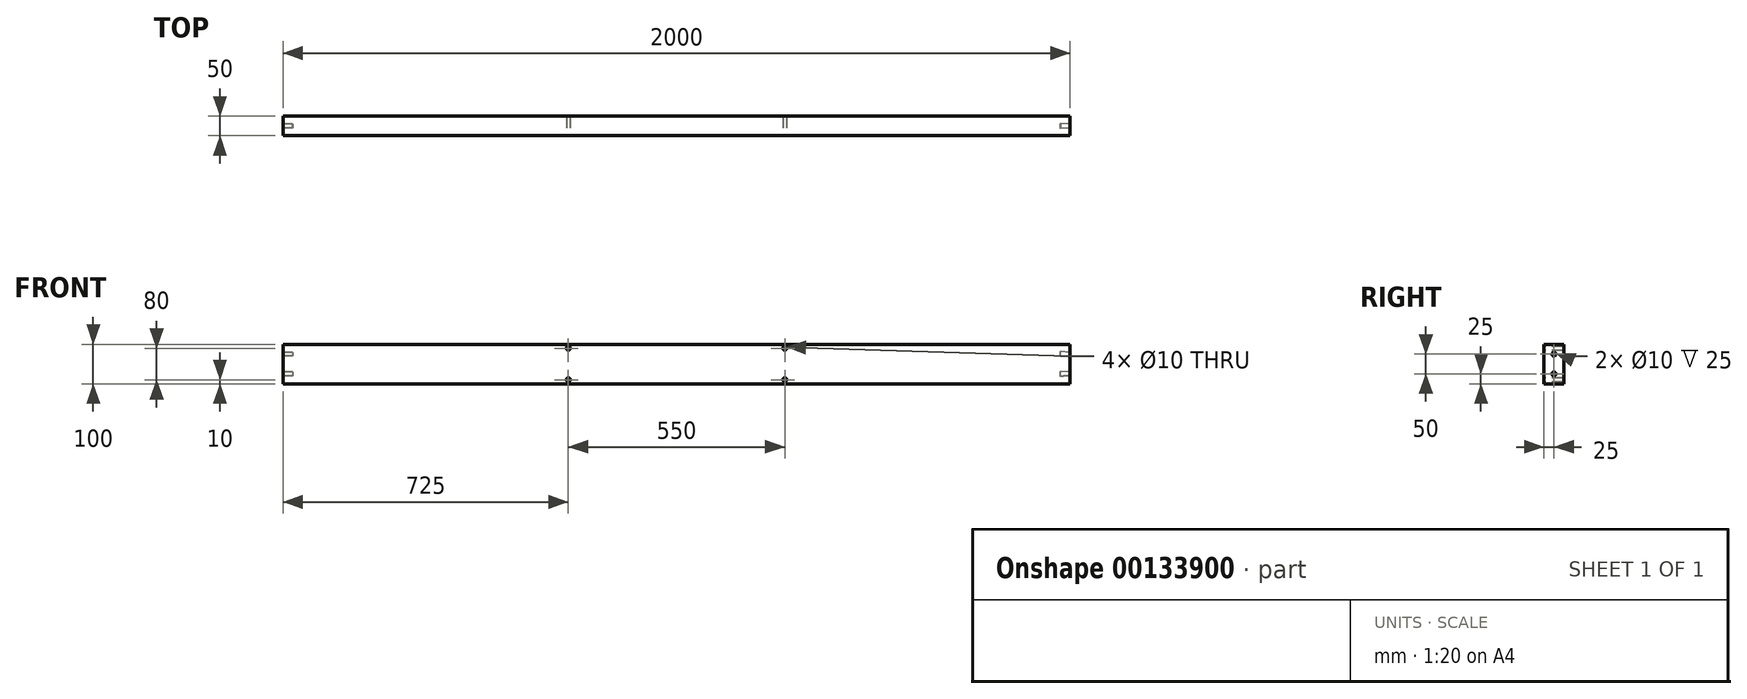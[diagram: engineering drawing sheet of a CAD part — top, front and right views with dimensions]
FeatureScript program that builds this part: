
annotation { "Feature Type Name" : "Feature", "Feature Type Description" : "" }
export const myFeature = defineFeature(function(context is Context, id is Id, definition is map)
    precondition{}
    {
        {
            var Q0;
            Q0=qCreatedBy(makeId("Front.planeOp"),FACE);
            var sketch = newSketch(context, id + "F0", { "sketchPlane" : qUnion([Q0])});
            skLineSegment(sketch, "E0.bottom", {"start": v(1000, -50) * mm, "end": v(-1000, -50) * mm});
            skLineSegment(sketch, "E0.top", {"start": v(1000, 50) * mm, "end": v(-1000, 50) * mm});
            skLineSegment(sketch, "E0.left", {"start": v(1000, -50) * mm, "end": v(1000, 50) * mm});
            skLineSegment(sketch, "E0.right", {"start": v(-1000, -50) * mm, "end": v(-1000, 50) * mm});
            skPoint(sketch, "E0.middle", {"position": v(0, 0) * mm});
            skSolve(sketch);
        }
        {
            var Q0;
            Q0=qSketchRegion(id+"F0",true);
            extrude(context, id + "F1", {"entities" : qUnion([Q0]), "depth" : 50 * mm});
        }
        {
            var Q0;
            Q0=makeQuery(id+"F1.opExtrude","SWEPT_FACE",FACE,{"disambiguationData":[OSD([sQuery(id+"F0.wireOp",EDGE,"E0.left")])]});
            var sketch = newSketch(context, id + "F2", { "sketchPlane" : qUnion([Q0])});
            skCircle(sketch, "E1", {"center": v(-25, 25) * mm, "radius": 5 * mm});
            skPoint(sketch, "E1.centerSnap0", {"position": v(-25, 50) * mm});
            skCircle(sketch, "E2", {"center": v(-25, -25) * mm, "radius": 5 * mm});
            skSolve(sketch);
        }
        {
            var Q0;
            Q0=makeQuery(id+"F1.opExtrude","SWEPT_FACE",FACE,{"disambiguationData":[OSD([sQuery(id+"F0.wireOp",EDGE,"E0.right")])]});
            var sketch = newSketch(context, id + "F3", { "sketchPlane" : qUnion([Q0])});
            skCircle(sketch, "E3", {"center": v(25, 25) * mm, "radius": 5 * mm});
            skPoint(sketch, "E3.centerSnap0", {"position": v(25, 50) * mm});
            skCircle(sketch, "E4", {"center": v(25, -25) * mm, "radius": 5 * mm});
            skSolve(sketch);
        }
        {
            var Q0;
            Q0=makeQuery(id+"F3.imprint","IMPRINT",FACE,{"disambiguationData":[TD([[makeQuery(id+"F3.imprint","IMPRINT",EDGE,{"derivedFrom":sQuery(id+"F3.wireOp",EDGE,"E3")}),1.0]])]});
            var Q1;
            Q1=makeQuery(id+"F3.imprint","IMPRINT",FACE,{"disambiguationData":[TD([[makeQuery(id+"F3.imprint","IMPRINT",EDGE,{"derivedFrom":sQuery(id+"F3.wireOp",EDGE,"E4")}),1.0]])]});
            extrude(context, id + "F4", {"entities" : qUnion([Q0, Q1]), "operationType" : NewBodyOperationType.REMOVE, "oppositeDirection" : true, "depth" : 25 * mm});
        }
        {
            var Q0;
            Q0=makeQuery(id+"F2.imprint","IMPRINT",FACE,{"disambiguationData":[TD([[makeQuery(id+"F2.imprint","IMPRINT",EDGE,{"derivedFrom":sQuery(id+"F2.wireOp",EDGE,"E2")}),1.0]])]});
            var Q1;
            Q1=makeQuery(id+"F2.imprint","IMPRINT",FACE,{"disambiguationData":[TD([[makeQuery(id+"F2.imprint","IMPRINT",EDGE,{"derivedFrom":sQuery(id+"F2.wireOp",EDGE,"E1")}),1.0]])]});
            extrude(context, id + "F5", {"entities" : qUnion([Q0, Q1]), "operationType" : NewBodyOperationType.REMOVE, "oppositeDirection" : true, "depth" : 25 * mm, "hasDraft" : true, "draftAngle" : 3 * degree});
        }
        {
            var Q0;
            Q0=makeQuery(id+"F1.opExtrude","CAP_FACE",FACE,{"disambiguationData":[OSD([sQuery(id+"F0.wireOp",EDGE,"E0.bottom"),sQuery(id+"F0.wireOp",EDGE,"E0.top"),sQuery(id+"F0.wireOp",EDGE,"E0.left"),sQuery(id+"F0.wireOp",EDGE,"E0.right")])],"isStart":false});
            var sketch = newSketch(context, id + "F6", { "sketchPlane" : qUnion([Q0])});
            skCircle(sketch, "E5", {"center": v(-275, 40) * mm, "radius": 5 * mm});
            skCircle(sketch, "E6", {"center": v(-275, -40) * mm, "radius": 5 * mm});
            skCircle(sketch, "E7", {"center": v(275, 40) * mm, "radius": 5 * mm});
            skCircle(sketch, "E8", {"center": v(275, -40) * mm, "radius": 5 * mm});
            skSolve(sketch);
        }
        {
            var Q0;
            Q0=makeQuery(id+"F6.imprint","IMPRINT",FACE,{"disambiguationData":[TD([[makeQuery(id+"F6.imprint","IMPRINT",EDGE,{"derivedFrom":sQuery(id+"F6.wireOp",EDGE,"E5")}),1.0]])]});
            var Q1;
            Q1=makeQuery(id+"F6.imprint","IMPRINT",FACE,{"disambiguationData":[TD([[makeQuery(id+"F6.imprint","IMPRINT",EDGE,{"derivedFrom":sQuery(id+"F6.wireOp",EDGE,"E6")}),1.0]])]});
            var Q2;
            Q2=makeQuery(id+"F6.imprint","IMPRINT",FACE,{"disambiguationData":[TD([[makeQuery(id+"F6.imprint","IMPRINT",EDGE,{"derivedFrom":sQuery(id+"F6.wireOp",EDGE,"E7")}),1.0]])]});
            var Q3;
            Q3=makeQuery(id+"F6.imprint","IMPRINT",FACE,{"disambiguationData":[TD([[makeQuery(id+"F6.imprint","IMPRINT",EDGE,{"derivedFrom":sQuery(id+"F6.wireOp",EDGE,"E8")}),1.0]])]});
            extrude(context, id + "F7", {"entities" : qUnion([Q0, Q1, Q2, Q3]), "operationType" : NewBodyOperationType.REMOVE, "oppositeDirection" : true, "depth" : 50 * mm});
        }
    });
